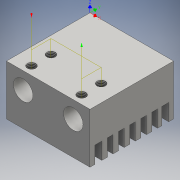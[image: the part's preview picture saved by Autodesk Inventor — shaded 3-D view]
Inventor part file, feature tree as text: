
AUTODESK INVENTOR PART (.ipt)
format: ipt  version: 2016 SP1 (Build 200210100, 210)  size: 623,616 bytes
history: native  units: mm
features: thread x9, extrude x7, sketch x7
ambient origin geometry x8: Origin, YZ Plane, XZ Plane, XY Plane, X Axis, Y Axis, Z Axis, Center Point
bodies: Solid1 (feature_tree)
feature tree (23):
  extrude  "Extrusion1"  Depth=30.0mm
  extrude  "Extrusion2"  Depth=15.0mm
  thread  "Thread3"  [1 undecoded]
  thread  "Thread4"  [1 undecoded]
  thread  "Thread5"  [1 undecoded]
  extrude  "Extrusion3"  Depth=5.0mm
  extrude  "Extrusion4"  Depth=17.0mm
  extrude  "Extrusion5"  Depth=3.0mm
  extrude  "Extrusion6"  Depth=18.0mm
  thread  "Thread1"  [1 undecoded]
  thread  "Thread2"  [1 undecoded]
  extrude  "Extrusion7"  Depth=10.0mm
  thread  "Thread6"  [1 undecoded]
  thread  "Thread7"  [1 undecoded]
  thread  "Thread8"  [1 undecoded]
  thread  "Thread9"  [1 undecoded]
  sketch  "Sketch1"  dims[d0=30.0mm d1=30.0mm]
  sketch  "Sketch2"  dims[d2=15.0mm d3=15.0mm d4=18.0mm d5=0.0mm d6=3.0mm d7=3.0mm]
  sketch  "Sketch3"  dims[d8=3.0mm d9=5.0mm]
  sketch  "Sketch4"  dims[d10=5.0mm d11=17.0mm]
  sketch  "Sketch5"  dims[d12=3.0mm d13=3.0mm]
  sketch  "Sketch6"  dims[d14=8.5mm d15=18.0mm d16=9.0mm d17=3.0mm]
  sketch  "Sketch7"  dims[d18=6.0mm d19=6.0mm d20=0.0mm d21=10.0mm d22=0.0mm d23=2.0mm d24=10.0mm d25=0.0mm d26=2.0mm d27=10.0mm d28=0.0mm d29=7.0mm d30=7.0mm d31=15.0mm d32=0.0mm d33=30.0mm d34=30.0mm d35=2.5mm d36=1.75mm d37=2.5mm d38=30.0mm d39=1.75mm d40=2.0mm d41=2.0mm d42=50.0mm d44=4.0mm d45=10.0mm d47=10.0mm d49=6.0mm d50=0.0mm d51=3.0mm d52=9.0mm d53=10.0mm d54=0.0mm d55=10.0mm d56=0.0mm d57=10.0mm d58=0.0mm d59=10.0mm d60=0.0mm d61=10.0mm d62=0.0mm d63=3.0mm d64=3.0mm d65=3.0mm d66=3.0mm d67=18.0mm d68=18.0mm d69=9.0mm d70=9.0mm d71=3.0mm d72=3.0mm d73=7.0mm d74=7.0mm d75=6.0mm d76=0.0mm d77=10.0mm d78=0.0mm d79=10.0mm d80=0.0mm d81=10.0mm d82=0.0mm d83=10.0mm d84=0.0mm]
note: 9 required parameter values undecoded (feature->parameter linkage not recoverable at this tier; creation-order binding heuristic only, values carry confidence <= 0.55)
